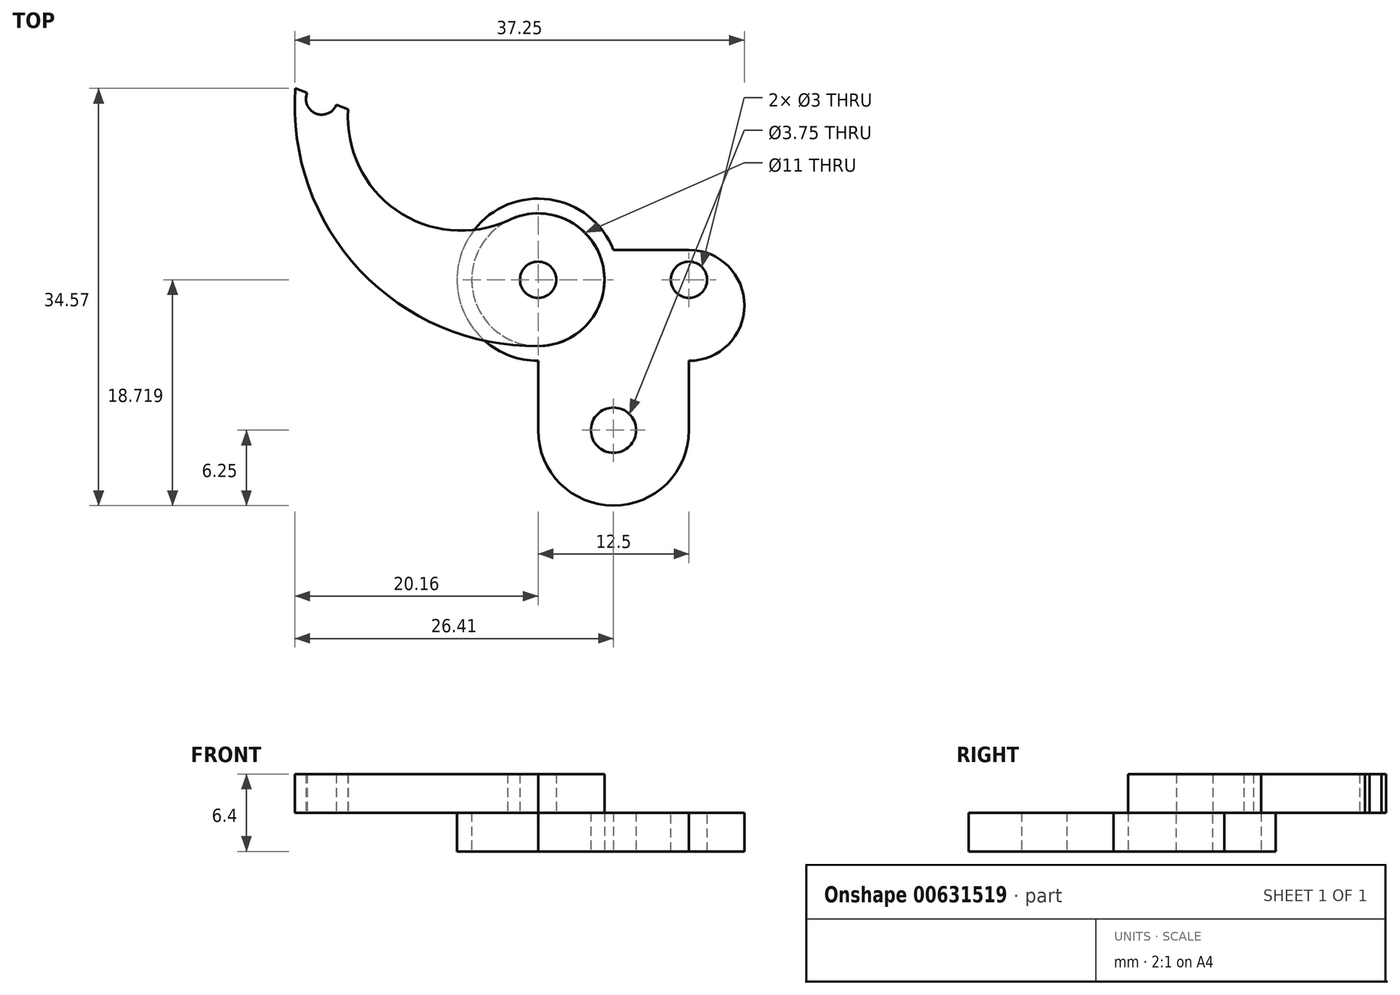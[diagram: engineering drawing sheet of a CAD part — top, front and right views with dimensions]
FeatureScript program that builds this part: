
annotation { "Feature Type Name" : "Feature", "Feature Type Description" : "" }
export const myFeature = defineFeature(function(context is Context, id is Id, definition is map)
    precondition{}
    {
        {
            var Q0;
            Q0=qCreatedBy(makeId("Top.planeOp"),FACE);
            var sketch = newSketch(context, id + "F0", { "sketchPlane" : qUnion([Q0])});
            skCircle(sketch, "E0", {"center": v(0, 0) * mm, "radius": 1.88 * mm});
            skLineSegment(sketch, "E1", {"start": v(-6.25, 5.75) * mm, "end": v(-6.25, 0) * mm});
            skLineSegment(sketch, "E2", {"start": v(6.25, 5.75) * mm, "end": v(6.25, 0) * mm});
            skArc(sketch, "E3", {"start": v(-6.25, 0) * mm, "mid": v(0, -6.25) * mm, "end": v(6.25, 0) * mm});
            skLineSegment(sketch, "E4", {"start": v(0, 0) * mm, "end": v(0, 19.69) * mm, "construction": true});
            skLineSegment(sketch, "E5", {"start": v(-6.25, 5.75) * mm, "end": v(6.25, 5.75) * mm, "construction": true});
            skArc(sketch, "E6", {"start": v(-6.25, 19.19) * mm, "mid": v(-12.97, 12.47) * mm, "end": v(-6.25, 5.75) * mm});
            skArc(sketch, "E7", {"start": v(6.25, 5.75) * mm, "mid": v(10.84, 10.34) * mm, "end": v(6.25, 14.93) * mm});
            skLineSegment(sketch, "E8", {"start": v(6.25, 14.93) * mm, "end": v(0, 14.93) * mm});
            skArc(sketch, "E9", {"start": v(-6.25, 19.19) * mm, "mid": v(-2.47, 18.02) * mm, "end": v(0, 14.93) * mm});
            skCircle(sketch, "E10", {"center": v(-6.25, 12.47) * mm, "radius": 5.5 * mm});
            skCircle(sketch, "E11", {"center": v(-6.25, 12.47) * mm, "radius": 1.5 * mm, "construction": true});
            skCircle(sketch, "E12.MirrorC", {"center": v(6.25, 12.47) * mm, "radius": 1.5 * mm, "construction": true});
            skSolve(sketch);
        }
        {
            var Q0;
            Q0 = qSketchRegion(id + "F0", true);
            extrude(context, id + "F1", {"entities" : qUnion([Q0]), "depth" : 3.2 * mm, "offsetDistance" : 25 * mm});
        }
        {
            var Q0;
            Q0=makeQuery(id+"F1.opExtrude","CAP_FACE",FACE,{"disambiguationData":[OSD([sQuery(id+"F0.wireOp",EDGE,"E0"),sQuery(id+"F0.wireOp",EDGE,"E1"),sQuery(id+"F0.wireOp",EDGE,"E2"),sQuery(id+"F0.wireOp",EDGE,"E3"),sQuery(id+"F0.wireOp",EDGE,"E6"),sQuery(id+"F0.wireOp",EDGE,"E7"),sQuery(id+"F0.wireOp",EDGE,"E8"),sQuery(id+"F0.wireOp",EDGE,"E9"),sQuery(id+"F0.wireOp",EDGE,"E10")])],"isStart":false});
            var sketch = newSketch(context, id + "F2", { "sketchPlane" : qUnion([Q0])});
            skCircle(sketch, "E13.0", {"center": v(6.25, 12.47) * mm, "radius": 1.5 * mm});
            skSolve(sketch);
        }
        {
            var Q0;
            Q0=makeQuery(id+"F1.opExtrude","CAP_FACE",FACE,{"disambiguationData":[OSD([sQuery(id+"F0.wireOp",EDGE,"E0"),sQuery(id+"F0.wireOp",EDGE,"E1"),sQuery(id+"F0.wireOp",EDGE,"E2"),sQuery(id+"F0.wireOp",EDGE,"E3"),sQuery(id+"F0.wireOp",EDGE,"E6"),sQuery(id+"F0.wireOp",EDGE,"E7"),sQuery(id+"F0.wireOp",EDGE,"E8"),sQuery(id+"F0.wireOp",EDGE,"E9"),sQuery(id+"F0.wireOp",EDGE,"E10")])],"isStart":false});
            var sketch = newSketch(context, id + "F3", { "sketchPlane" : qUnion([Q0])});
            skCircle(sketch, "E14", {"center": v(-6.25, 12.47) * mm, "radius": 1.5 * mm});
            skArc(sketch, "E15", {"start": v(-6.25, 6.97) * mm, "mid": v(-0.9, 13.77) * mm, "end": v(-8.77, 17.36) * mm});
            skLineSegment(sketch, "E16", {"start": v(-26.36, 28.32) * mm, "end": v(-25.39, 27.94) * mm});
            skArc(sketch, "E17", {"start": v(-25.39, 27.94) * mm, "mid": v(-24.65, 26.24) * mm, "end": v(-22.95, 26.97) * mm});
            skArc(sketch, "E18", {"start": v(-26.36, 28.32) * mm, "mid": v(-21, 13.23) * mm, "end": v(-6.25, 6.97) * mm});
            skArc(sketch, "E19", {"start": v(-21.98, 26.59) * mm, "mid": v(-18, 18.23) * mm, "end": v(-8.77, 17.36) * mm});
            skLineSegment(sketch, "E20.trimOffspring", {"start": v(-22.95, 26.97) * mm, "end": v(-21.98, 26.59) * mm});
            skLineSegment(sketch, "E21", {"start": v(-0.75, 12.66) * mm, "end": v(-0.9, 28.76) * mm, "construction": true});
            skPoint(sketch, "E21.endSnap0", {"position": v(-0.9, 13.77) * mm});
            skSolve(sketch);
        }
        {
            var Q0;
            Q0=makeQuery(id+"F3.imprint","IMPRINT",FACE,{"disambiguationData":[TD([[makeQuery(id+"F3.imprint","IMPRINT",EDGE,{"derivedFrom":sQuery(id+"F3.wireOp",EDGE,"E14")}),-1.0]])]});
            var Q1;
            {var subQ0=sQuery(id+"F3.wireOp",EDGE,"E18");var subQ1=sQuery(id+"F3.wireOp",EDGE,"E15");var subQ2=makeQuery(id+"F1.opExtrude","CAP_EDGE",EDGE,{"disambiguationData":[OSD([sQuery(id+"F0.wireOp",EDGE,"E10")])],"isStart":false});var subQ3=makeQuery(id+"F3.imprint","INTERSECT",VERTEX,{"derivedFrom":[subQ2,subQ1,subQ0]});Q1=makeQuery(id+"F3.imprint","IMPRINT",FACE,{"disambiguationData":[TD([[makeQuery(id+"F3.imprint","IMPRINT",EDGE,{"disambiguationData":[TD([[subQ3,1.0]])],"derivedFrom":subQ0}),1.0]])]});}
            var Q2;
            {var subQ5=sQuery(id+"F3.wireOp",EDGE,"E16");Q2=makeQuery(id+"F3.imprint","IMPRINT",FACE,{"disambiguationData":[TD([[makeQuery(id+"F3.imprint","IMPRINT",EDGE,{"derivedFrom":subQ5}),-1.0]])]});}
            extrude(context, id + "F4", {"entities" : qUnion([Q0, Q1, Q2]), "depth" : 3.2 * mm, "offsetDistance" : 25 * mm});
        }
        {
            var Q0;
            Q0 = qSketchRegion(id + "F2", true);
            var Q1;
            Q1=makeQuery(id+"F1.opExtrude","CAP_FACE",FACE,{"disambiguationData":[OSD([sQuery(id+"F0.wireOp",EDGE,"E0"),sQuery(id+"F0.wireOp",EDGE,"E1"),sQuery(id+"F0.wireOp",EDGE,"E2"),sQuery(id+"F0.wireOp",EDGE,"E3"),sQuery(id+"F0.wireOp",EDGE,"E6"),sQuery(id+"F0.wireOp",EDGE,"E7"),sQuery(id+"F0.wireOp",EDGE,"E8"),sQuery(id+"F0.wireOp",EDGE,"E9"),sQuery(id+"F0.wireOp",EDGE,"E10")])],"isStart":true});
            extrude(context, id + "F5", {"entities" : qUnion([Q0]), "operationType" : NewBodyOperationType.REMOVE, "endBound" : BoundingType.UP_TO_SURFACE, "oppositeDirection" : true, "depth" : 25 * mm, "endBoundEntityFace" : qUnion([Q1]), "offsetDistance" : 25 * mm});
        }
    });
